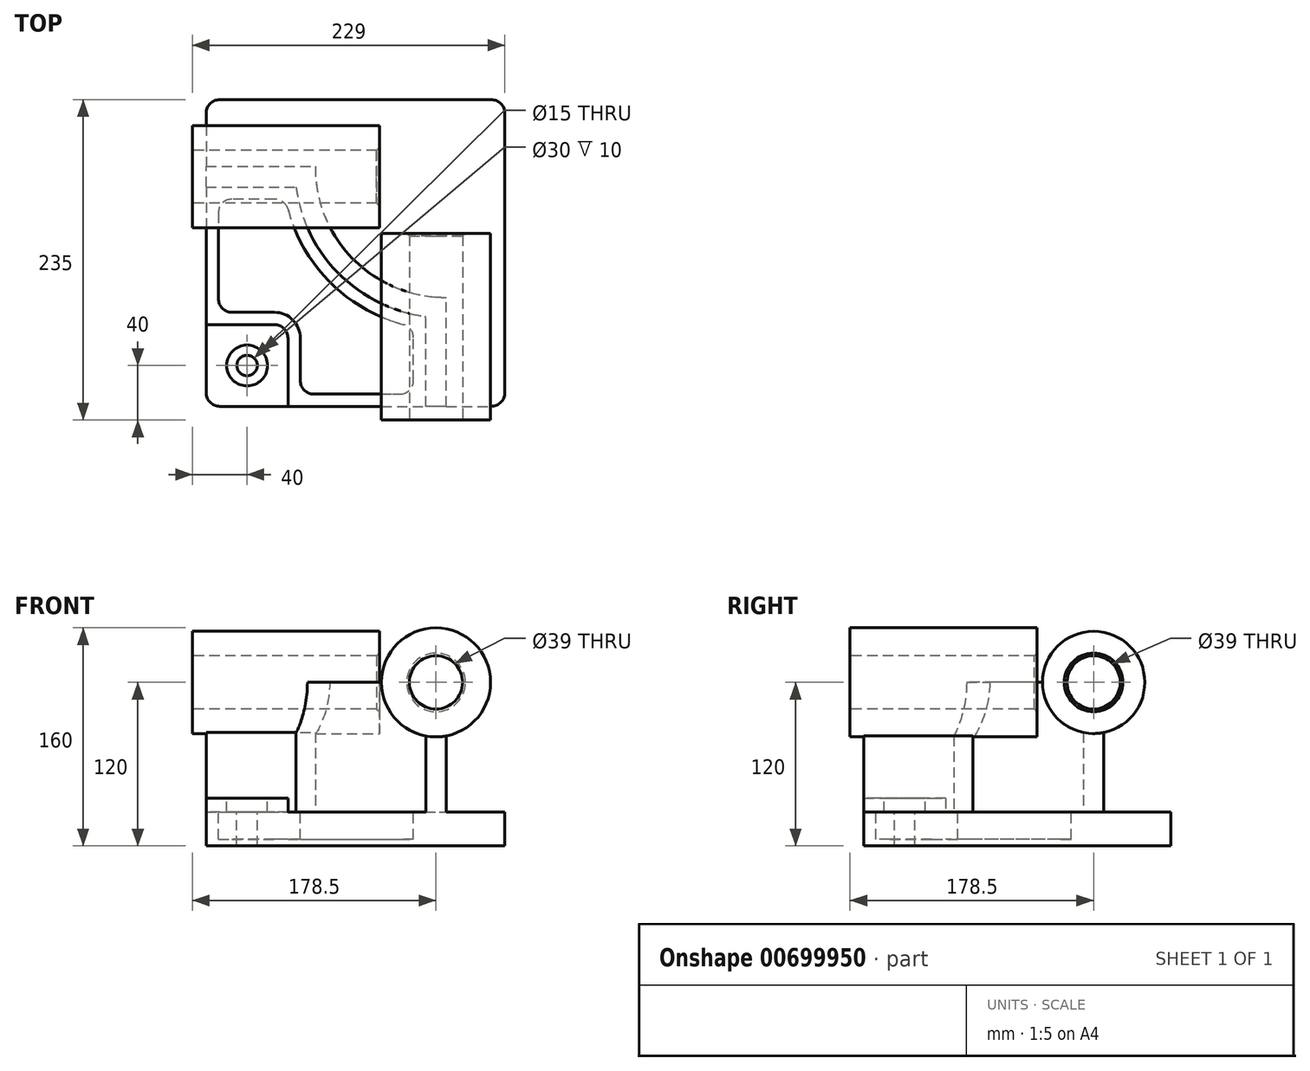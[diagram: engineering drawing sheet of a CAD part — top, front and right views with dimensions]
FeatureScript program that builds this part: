
annotation { "Feature Type Name" : "Feature", "Feature Type Description" : "" }
export const myFeature = defineFeature(function(context is Context, id is Id, definition is map)
    precondition{}
    {
        {
            var Q0;
            Q0=qCreatedBy(makeId("Top.planeOp"),FACE);
            var sketch = newSketch(context, id + "F0", { "sketchPlane" : qUnion([Q0])});
            skLineSegment(sketch, "E0.bottom", {"start": v(-109.5, 112.5) * mm, "end": v(109.5, 112.5) * mm});
            skLineSegment(sketch, "E0.top", {"start": v(-109.5, -112.5) * mm, "end": v(109.5, -112.5) * mm});
            skLineSegment(sketch, "E0.left", {"start": v(-109.5, 112.5) * mm, "end": v(-109.5, -112.5) * mm});
            skLineSegment(sketch, "E0.right", {"start": v(109.5, 112.5) * mm, "end": v(109.5, -112.5) * mm});
            skPoint(sketch, "E0.middle", {"position": v(0, 0) * mm});
            skSolve(sketch);
        }
        {
            var Q0;
            Q0 = qSketchRegion(id + "F0", true);
            extrude(context, id + "F1", {"entities" : qUnion([Q0]), "depth" : 25 * mm, "offsetDistance" : 25.4 * mm});
        }
        {
            var Q0;
            Q0=makeQuery(id+"F1.opExtrude","CAP_FACE",FACE,{"disambiguationData":[OSD([sQuery(id+"F0.wireOp",EDGE,"E0.bottom"),sQuery(id+"F0.wireOp",EDGE,"E0.top"),sQuery(id+"F0.wireOp",EDGE,"E0.left"),sQuery(id+"F0.wireOp",EDGE,"E0.right")])],"isStart":false});
            var sketch = newSketch(context, id + "F2", { "sketchPlane" : qUnion([Q0])});
            skLineSegment(sketch, "E1", {"start": v(-109.5, 63.5) * mm, "end": v(-29.5, 63.5) * mm});
            skLineSegment(sketch, "E2", {"start": v(66.5, -112.5) * mm, "end": v(66.5, -32.5) * mm});
            skArc(sketch, "E3", {"start": v(-29.5, 63.5) * mm, "mid": v(-1.59, -4.59) * mm, "end": v(66.5, -32.5) * mm});
            skLineSegment(sketch, "E4", {"start": v(65.8, 62.8) * mm, "end": v(66.5, -32.5) * mm, "construction": true});
            skLineSegment(sketch, "E5", {"start": v(65.8, 62.8) * mm, "end": v(-29.5, 63.5) * mm, "construction": true});
            skLineSegment(sketch, "E6.0", {"start": v(51.5, -112.5) * mm, "end": v(51.5, -46.57) * mm});
            skArc(sketch, "E6.1", {"start": v(-43.57, 48.5) * mm, "mid": v(-12.2, -15.2) * mm, "end": v(51.5, -46.57) * mm});
            skLineSegment(sketch, "E6.2", {"start": v(-109.5, 48.5) * mm, "end": v(-43.57, 48.5) * mm});
            skLineSegment(sketch, "E7.0", {"start": v(51.5, -112.5) * mm, "end": v(109.5, -112.5) * mm});
            skLineSegment(sketch, "E8.0", {"start": v(-109.5, 112.5) * mm, "end": v(-109.5, 48.5) * mm});
            skPoint(sketch, "E9.orphan", {"position": v(-109.5, -112.5) * mm});
            skSolve(sketch);
        }
        {
            var Q0;
            {var subQ2=sQuery(id+"F2.wireOp",EDGE,"E1");Q0=makeQuery(id+"F2.imprint","IMPRINT",FACE,{"disambiguationData":[TD([[makeQuery(id+"F2.imprint","IMPRINT",EDGE,{"derivedFrom":subQ2}),-1.0]])]});}
            extrude(context, id + "F3", {"entities" : qUnion([Q0]), "operationType" : NewBodyOperationType.ADD, "depth" : 95 * mm, "offsetDistance" : 25.4 * mm});
        }
        {
            var Q0;
            Q0=makeQuery(id+"F3.boolean.opBoolean","MERGE",FACE,{"derivedFrom":[makeQuery(id+"F1.opExtrude","SWEPT_FACE",FACE,{"disambiguationData":[OSD([sQuery(id+"F0.wireOp",EDGE,"E0.left")])]}),makeQuery(id+"F3.opExtrude","SWEPT_FACE",FACE,{"disambiguationData":[OSD([sQuery(id+"F2.wireOp",EDGE,"E8.0")])]})]});
            var sketch = newSketch(context, id + "F4", { "sketchPlane" : qUnion([Q0])});
            skCircle(sketch, "E10", {"center": v(-56, 120) * mm, "radius": 37.5 * mm});
            skSolve(sketch);
        }
        {
            var Q0;
            Q0 = qSketchRegion(id + "F4", true);
            extrude(context, id + "F5", {"entities" : qUnion([Q0]), "operationType" : NewBodyOperationType.ADD, "depth" : 10 * mm, "offsetDistance" : 25.4 * mm, "hasSecondDirection" : true, "secondDirectionOppositeDirection" : true, "secondDirectionDepth" : 127 * mm});
        }
        {
            var Q0;
            Q0=makeQuery(id+"F3.boolean.opBoolean","MERGE",FACE,{"derivedFrom":[makeQuery(id+"F1.opExtrude","SWEPT_FACE",FACE,{"disambiguationData":[OSD([sQuery(id+"F0.wireOp",EDGE,"E0.top")])]}),makeQuery(id+"F3.opExtrude","SWEPT_FACE",FACE,{"disambiguationData":[OSD([sQuery(id+"F2.wireOp",EDGE,"E7.0")])]})]});
            var sketch = newSketch(context, id + "F6", { "sketchPlane" : qUnion([Q0])});
            skCircle(sketch, "E11", {"center": v(59, 120) * mm, "radius": 40 * mm});
            skSolve(sketch);
        }
        {
            var Q0;
            Q0 = qSketchRegion(id + "F6", true);
            extrude(context, id + "F7", {"entities" : qUnion([Q0]), "operationType" : NewBodyOperationType.ADD, "depth" : 10 * mm, "offsetDistance" : 25.4 * mm, "hasSecondDirection" : true, "secondDirectionOppositeDirection" : true, "secondDirectionDepth" : 127 * mm});
        }
        {
            var Q0;
            {var subQ0=sQuery(id+"F0.wireOp",EDGE,"E0.left");var subQ1=sQuery(id+"F0.wireOp",EDGE,"E0.top");Q0=makeQuery(id+"F3.boolean.opBoolean","SPLIT",FACE,{"disambiguationData":[TD([makeQuery(id+"F3.opExtrude","SWEPT_FACE",FACE,{"disambiguationData":[OSD([sQuery(id+"F2.wireOp",EDGE,"E6.0")])]})])],"derivedFrom":makeQuery(id+"F1.opExtrude","CAP_FACE",FACE,{"disambiguationData":[OSD([sQuery(id+"F0.wireOp",EDGE,"E0.bottom"),subQ1,subQ0,sQuery(id+"F0.wireOp",EDGE,"E0.right")])],"isStart":false})});}
            var sketch = newSketch(context, id + "F8", { "sketchPlane" : qUnion([Q0])});
            skLineSegment(sketch, "E12.bottom", {"start": v(-109.5, -112.5) * mm, "end": v(-49.5, -112.5) * mm});
            skLineSegment(sketch, "E12.top", {"start": v(-109.5, -52.5) * mm, "end": v(-49.5, -52.5) * mm});
            skLineSegment(sketch, "E12.left", {"start": v(-109.5, -112.5) * mm, "end": v(-109.5, -52.5) * mm});
            skLineSegment(sketch, "E12.right", {"start": v(-49.5, -112.5) * mm, "end": v(-49.5, -52.5) * mm});
            skSolve(sketch);
        }
        {
            var Q0;
            Q0 = qSketchRegion(id + "F8", true);
            extrude(context, id + "F9", {"entities" : qUnion([Q0]), "operationType" : NewBodyOperationType.ADD, "depth" : 10 * mm, "offsetDistance" : 25.4 * mm});
        }
        {
            var Q0;
            Q0=makeQuery(id+"F9.opExtrude","SWEPT_EDGE",EDGE,{"disambiguationData":[OSD([sQuery(id+"F8.wireOp",EDGE,"E12.top"),sQuery(id+"F8.wireOp",EDGE,"E12.right")])]});
            fillet(context, id + "F10", {"entities" : qUnion([Q0]), "radius" : 10 * mm, "tangentPropagation" : true, "allowEdgeOverflow" : false});
        }
        {
            var Q0;
            {var subQ0=sQuery(id+"F0.wireOp",EDGE,"E0.left");var subQ1=sQuery(id+"F0.wireOp",EDGE,"E0.top");Q0=makeQuery(id+"F3.boolean.opBoolean","SPLIT",FACE,{"disambiguationData":[TD([makeQuery(id+"F3.opExtrude","SWEPT_FACE",FACE,{"disambiguationData":[OSD([sQuery(id+"F2.wireOp",EDGE,"E6.0")])]})])],"derivedFrom":makeQuery(id+"F1.opExtrude","CAP_FACE",FACE,{"disambiguationData":[OSD([sQuery(id+"F0.wireOp",EDGE,"E0.bottom"),subQ1,subQ0,sQuery(id+"F0.wireOp",EDGE,"E0.right")])],"isStart":false})});}
            var sketch = newSketch(context, id + "F11", { "sketchPlane" : qUnion([Q0])});
            skLineSegment(sketch, "E13.0", {"start": v(-51.2, 39.5) * mm, "end": v(-100.5, 39.5) * mm});
            skArc(sketch, "E13.1", {"start": v(42.5, -54.2) * mm, "mid": v(-18.56, -21.56) * mm, "end": v(-51.2, 39.5) * mm});
            skLineSegment(sketch, "E13.2", {"start": v(-100.5, 39.5) * mm, "end": v(-100.5, -43.5) * mm});
            skLineSegment(sketch, "E13.3", {"start": v(42.5, -103.5) * mm, "end": v(42.5, -54.2) * mm});
            skLineSegment(sketch, "E13.4", {"start": v(-100.5, -43.5) * mm, "end": v(-59.5, -43.5) * mm});
            skArc(sketch, "E13.5", {"start": v(-59.5, -43.5) * mm, "mid": v(-46.06, -49.06) * mm, "end": v(-40.5, -62.5) * mm});
            skLineSegment(sketch, "E13.6", {"start": v(-40.5, -62.5) * mm, "end": v(-40.5, -103.5) * mm});
            skLineSegment(sketch, "E13.7", {"start": v(-40.5, -103.5) * mm, "end": v(42.5, -103.5) * mm});
            skSolve(sketch);
        }
        {
            var Q0;
            Q0 = qSketchRegion(id + "F11", true);
            extrude(context, id + "F12", {"entities" : qUnion([Q0]), "operationType" : NewBodyOperationType.REMOVE, "oppositeDirection" : true, "depth" : 20 * mm, "offsetDistance" : 25.4 * mm});
        }
        {
            var Q0;
            Q0=makeQuery(id+"F9.opExtrude","CAP_FACE",FACE,{"disambiguationData":[OSD([sQuery(id+"F8.wireOp",EDGE,"E12.bottom"),sQuery(id+"F8.wireOp",EDGE,"E12.top"),sQuery(id+"F8.wireOp",EDGE,"E12.left"),sQuery(id+"F8.wireOp",EDGE,"E12.right")])],"isStart":false});
            var sketch = newSketch(context, id + "F13", { "sketchPlane" : qUnion([Q0])});
            skCircle(sketch, "E14", {"center": v(-79.5, -82.5) * mm, "radius": 15 * mm});
            skSolve(sketch);
        }
        {
            var Q0;
            Q0=sQuery(id+"F13.wireOp",VERTEX,"E14.center");
            var Q1;
            Q1=makeQuery(id+"F1.opExtrude","SWEPT_BODY",BODY,{"disambiguationData":[OSD([sQuery(id+"F0.wireOp",EDGE,"E0.bottom"),sQuery(id+"F0.wireOp",EDGE,"E0.top"),sQuery(id+"F0.wireOp",EDGE,"E0.left"),sQuery(id+"F0.wireOp",EDGE,"E0.right")])]});
            hole(context, id + "F14", {"style" : HoleStyle.C_BORE, "endStyle" : HoleEndStyle.THROUGH, "holeDiameter" : 15 * mm, "cBoreDiameter" : 30 * mm, "cBoreDepth" : 10 * mm, "majorDiameter" : 6.35 * mm, "isTappedThrough" : true, "tappedDepth" : 12.7 * mm, "tapClearance" : 3, "locations" : qUnion([Q0]), "scope" : qUnion([Q1])});
        }
        {
            var Q0;
            Q0=makeQuery(id+"F12.boolean.opBoolean","COPY",EDGE,{"derivedFrom":makeQuery(id+"F12.opExtrude","SWEPT_EDGE",EDGE,{"disambiguationData":[OSD([sQuery(id+"F11.wireOp",EDGE,"E13.1"),sQuery(id+"F11.wireOp",EDGE,"E13.3")])]})});
            var Q1;
            Q1=makeQuery(id+"F12.boolean.opBoolean","COPY",EDGE,{"derivedFrom":makeQuery(id+"F12.opExtrude","SWEPT_EDGE",EDGE,{"disambiguationData":[OSD([sQuery(id+"F11.wireOp",EDGE,"E13.0"),sQuery(id+"F11.wireOp",EDGE,"E13.1")])]})});
            var Q2;
            Q2=makeQuery(id+"F12.boolean.opBoolean","COPY",EDGE,{"derivedFrom":makeQuery(id+"F12.opExtrude","SWEPT_EDGE",EDGE,{"disambiguationData":[OSD([sQuery(id+"F11.wireOp",EDGE,"E13.3"),sQuery(id+"F11.wireOp",EDGE,"E13.7")])]})});
            var Q3;
            Q3=makeQuery(id+"F12.boolean.opBoolean","COPY",EDGE,{"derivedFrom":makeQuery(id+"F12.opExtrude","SWEPT_EDGE",EDGE,{"disambiguationData":[OSD([sQuery(id+"F11.wireOp",EDGE,"E13.6"),sQuery(id+"F11.wireOp",EDGE,"E13.7")])]})});
            var Q4;
            Q4=makeQuery(id+"F12.boolean.opBoolean","COPY",EDGE,{"derivedFrom":makeQuery(id+"F12.opExtrude","SWEPT_EDGE",EDGE,{"disambiguationData":[OSD([sQuery(id+"F11.wireOp",EDGE,"E13.0"),sQuery(id+"F11.wireOp",EDGE,"E13.2")])]})});
            var Q5;
            Q5=makeQuery(id+"F12.boolean.opBoolean","COPY",EDGE,{"derivedFrom":makeQuery(id+"F12.opExtrude","SWEPT_EDGE",EDGE,{"disambiguationData":[OSD([sQuery(id+"F11.wireOp",EDGE,"E13.2"),sQuery(id+"F11.wireOp",EDGE,"E13.4")])]})});
            fillet(context, id + "F15", {"entities" : qUnion([Q0, Q1, Q2, Q3, Q4, Q5]), "radius" : 10 * mm, "tangentPropagation" : true, "allowEdgeOverflow" : false});
        }
        {
            var Q0;
            Q0=makeQuery(id+"F5.opExtrude","CAP_FACE",FACE,{"disambiguationData":[OSD([sQuery(id+"F4.wireOp",EDGE,"E10")])],"isStart":false});
            var sketch = newSketch(context, id + "F16", { "sketchPlane" : qUnion([Q0])});
            skCircle(sketch, "E15", {"center": v(-56, 120) * mm, "radius": 19.5 * mm});
            skSolve(sketch);
        }
        {
            var Q0;
            Q0 = qSketchRegion(id + "F16", true);
            extrude(context, id + "F17", {"entities" : qUnion([Q0]), "operationType" : NewBodyOperationType.REMOVE, "endBound" : BoundingType.THROUGH_ALL, "oppositeDirection" : true, "depth" : 25.4 * mm, "offsetDistance" : 25.4 * mm});
        }
        {
            var Q0;
            Q0=makeQuery(id+"F7.opExtrude","CAP_FACE",FACE,{"disambiguationData":[OSD([sQuery(id+"F6.wireOp",EDGE,"E11")])],"isStart":false});
            var sketch = newSketch(context, id + "F18", { "sketchPlane" : qUnion([Q0])});
            skCircle(sketch, "E16", {"center": v(59, 120) * mm, "radius": 19.5 * mm});
            skSolve(sketch);
        }
        {
            var Q0;
            Q0 = qSketchRegion(id + "F18", true);
            extrude(context, id + "F19", {"entities" : qUnion([Q0]), "operationType" : NewBodyOperationType.REMOVE, "endBound" : BoundingType.THROUGH_ALL, "oppositeDirection" : true, "depth" : 25.4 * mm, "offsetDistance" : 25.4 * mm});
        }
        {
            var Q0;
            Q0=makeQuery(id+"F17.boolean.opBoolean","COPY",EDGE,{"derivedFrom":makeQuery(id+"F17.opExtrude","CAP_EDGE",EDGE,{"disambiguationData":[OSD([sQuery(id+"F16.wireOp",EDGE,"E15")])],"isStart":true})});
            var Q1;
            Q1=makeQuery(id+"F19.boolean.opBoolean","COPY",EDGE,{"derivedFrom":makeQuery(id+"F19.opExtrude","CAP_EDGE",EDGE,{"disambiguationData":[OSD([sQuery(id+"F18.wireOp",EDGE,"E16")])],"isStart":true})});
            var Q2;
            Q2=makeQuery(id+"F19.boolean.opBoolean","INTERSECT",EDGE,{"derivedFrom":[makeQuery(id+"F7.opExtrude","CAP_FACE",FACE,{"disambiguationData":[OSD([sQuery(id+"F6.wireOp",EDGE,"E11")])],"isStart":true}),makeQuery(id+"F19.opExtrude","SWEPT_FACE",FACE,{"disambiguationData":[OSD([sQuery(id+"F18.wireOp",EDGE,"E16")])]})]});
            var Q3;
            Q3=makeQuery(id+"F17.boolean.opBoolean","INTERSECT",EDGE,{"derivedFrom":[makeQuery(id+"F5.opExtrude","CAP_FACE",FACE,{"disambiguationData":[OSD([sQuery(id+"F4.wireOp",EDGE,"E10")])],"isStart":true}),makeQuery(id+"F17.opExtrude","SWEPT_FACE",FACE,{"disambiguationData":[OSD([sQuery(id+"F16.wireOp",EDGE,"E15")])]})]});
            chamfer(context, id + "F20", {"entities" : qUnion([Q0, Q1, Q2, Q3]), "width" : 2 * mm, "tangentPropagation" : true});
        }
        {
            var Q0;
            Q0=makeQuery(id+"F9.boolean.opBoolean","MERGE",EDGE,{"derivedFrom":[makeQuery(id+"F1.opExtrude","SWEPT_EDGE",EDGE,{"disambiguationData":[OSD([sQuery(id+"F0.wireOp",EDGE,"E0.top"),sQuery(id+"F0.wireOp",EDGE,"E0.left")])]}),makeQuery(id+"F9.opExtrude","SWEPT_EDGE",EDGE,{"disambiguationData":[OSD([sQuery(id+"F8.wireOp",EDGE,"E12.bottom"),sQuery(id+"F8.wireOp",EDGE,"E12.left")])]})]});
            var Q1;
            Q1=makeQuery(id+"F1.opExtrude","SWEPT_EDGE",EDGE,{"disambiguationData":[OSD([sQuery(id+"F0.wireOp",EDGE,"E0.top"),sQuery(id+"F0.wireOp",EDGE,"E0.right")])]});
            var Q2;
            Q2=makeQuery(id+"F1.opExtrude","SWEPT_EDGE",EDGE,{"disambiguationData":[OSD([sQuery(id+"F0.wireOp",EDGE,"E0.bottom"),sQuery(id+"F0.wireOp",EDGE,"E0.right")])]});
            var Q3;
            Q3=makeQuery(id+"F1.opExtrude","SWEPT_EDGE",EDGE,{"disambiguationData":[OSD([sQuery(id+"F0.wireOp",EDGE,"E0.bottom"),sQuery(id+"F0.wireOp",EDGE,"E0.left")])]});
            fillet(context, id + "F21", {"entities" : qUnion([Q0, Q1, Q2, Q3]), "radius" : 10 * mm, "tangentPropagation" : true, "allowEdgeOverflow" : false});
        }
    });
